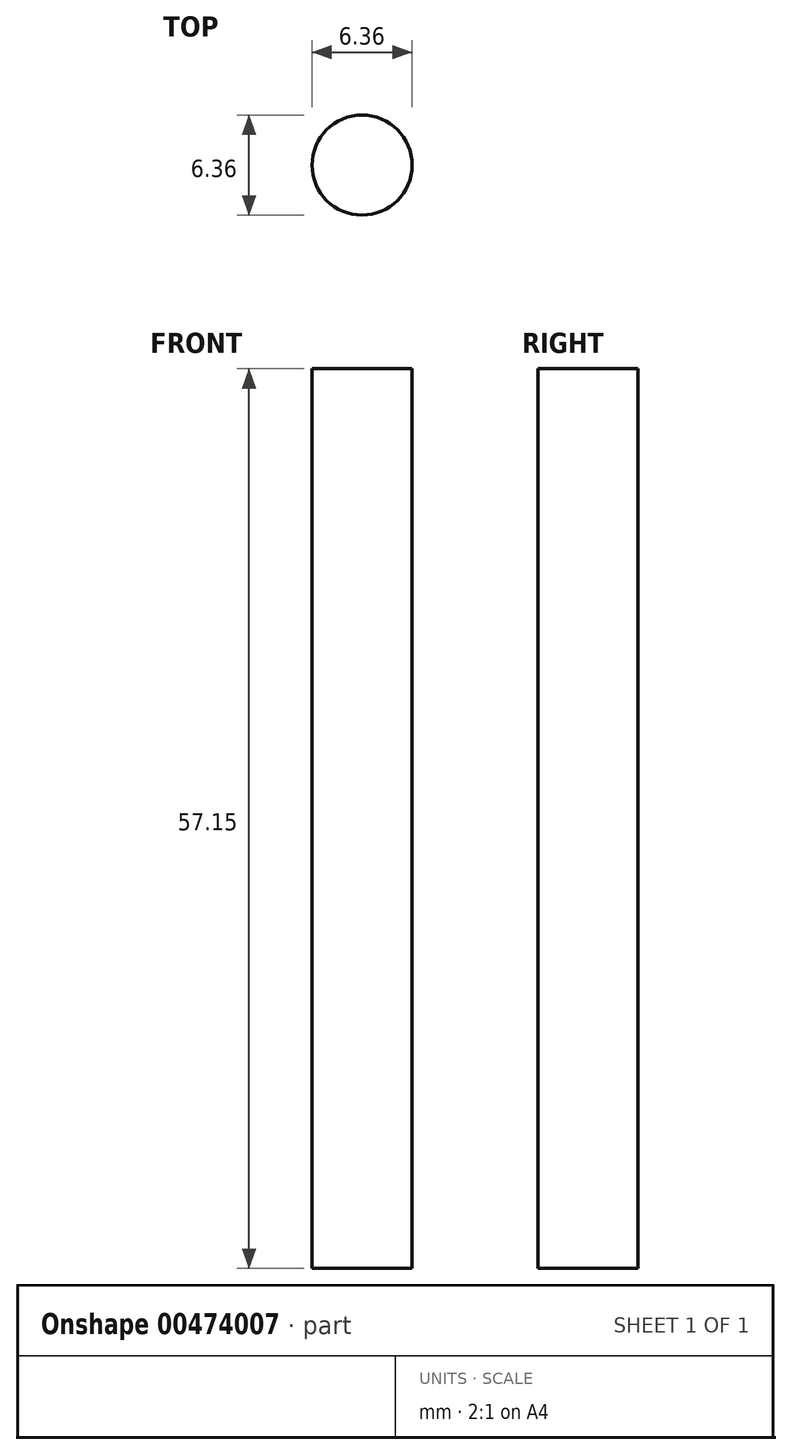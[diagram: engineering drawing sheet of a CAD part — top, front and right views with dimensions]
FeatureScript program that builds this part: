
annotation { "Feature Type Name" : "Feature", "Feature Type Description" : "" }
export const myFeature = defineFeature(function(context is Context, id is Id, definition is map)
    precondition{}
    {
        {
            var Q0;
            Q0=qCreatedBy(makeId("Top.planeOp"),FACE);
            var sketch = newSketch(context, id + "F0", { "sketchPlane" : qUnion([Q0])});
            skCircle(sketch, "E0", {"center": v(0, 0) * mm, "radius": 3.18 * mm});
            skSolve(sketch);
        }
        {
            var Q0;
            Q0 = qSketchRegion(id + "F0", true);
            extrude(context, id + "F1", {"entities" : qUnion([Q0]), "depth" : 57.15 * mm});
        }
    });
